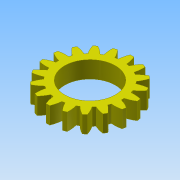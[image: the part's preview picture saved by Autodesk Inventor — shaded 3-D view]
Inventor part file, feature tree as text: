
AUTODESK INVENTOR PART (.ipt)
format: ipt  version: 2015 (Build 190159000, 159)  size: 246,784 bytes
history: native  units: mm (DEFAULTED — no unit token found)
features: plane x3, other x3, sketch x3, extrude x1, hole x1, projected_geometry x1
ambient origin geometry x8: Origin, YZ Plane, XZ Plane, XY Plane, X Axis, Y Axis, Z Axis, Center Point
bodies: Solid1 (feature_tree)
feature tree (12):
  extrude  "Extrusion1"  Depth=4.0mm TaperAngle=0.0deg
  plane  "Work Plane2"
  plane  "Work Plane8"
  plane  "Work Plane9"
  other  "Stirnzahnrad"
  hole  "Bohrung1"  [1 undecoded]
  sketch  "Sketch1"  dims[d0=20.0mm d1=4.0mm d2=0.0mm]
  sketch  "Sketch2"  dims[d3=18.0mm d4=10.0mm d5=0.0mm]
  other  "Srf1"
  sketch  "Skizze3"  dims[d16=18.0mm d17=0.0mm d34=1.745329mm d39=0.0mm d41=0.0mm d43=18.0mm d46=18.0mm d47=0.0mm d48=0.0mm d49=12.0mm d50=6.0mm d51=4.0mm d52=2.0mm d53=90.0deg d54=8.0mm d55=20.594885mm]
  projected_geometry  "Projizierte Kontur1"
  other  "Flankendurchmesser"
note: 1 required parameter value undecoded (feature->parameter linkage not recoverable at this tier; creation-order binding heuristic only, values carry confidence <= 0.55)
